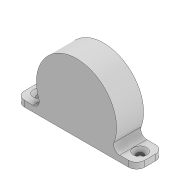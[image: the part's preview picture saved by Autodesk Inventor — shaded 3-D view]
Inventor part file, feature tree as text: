
AUTODESK INVENTOR PART (.ipt)
format: ipt  version: 2021 (Build 250183000, 183)  size: 147,456 bytes
history: native  units: mm
features: sketch x3, extrude x2, projected_geometry x2, other x1, fillet x1, hole x1, mirror x1
ambient origin geometry x8: Origin, YZ Plane, XZ Plane, XY Plane, X Axis, Y Axis, Z Axis, Center Point
bodies: Body1 (feature_tree)
feature tree (11):
  other  "Твердое тело1"
  extrude  "Выдавливание1"  Depth=3.0mm
  extrude  "Выдавливание2"  Depth=22.0mm
  fillet  "Сопряжение1"  Radius=14.0mm
  hole  "Отверстие2"  [1 undecoded]
  mirror  "Зеркальное отражение2"
  sketch  "Эскиз1"
  sketch  "Эскиз2"
  projected_geometry  "Спроецированная петля1"
  sketch  "Эскиз4"
  projected_geometry  "Спроецированная петля3"
note: 1 required parameter value undecoded (feature->parameter linkage not recoverable at this tier; creation-order binding heuristic only, values carry confidence <= 0.55)
